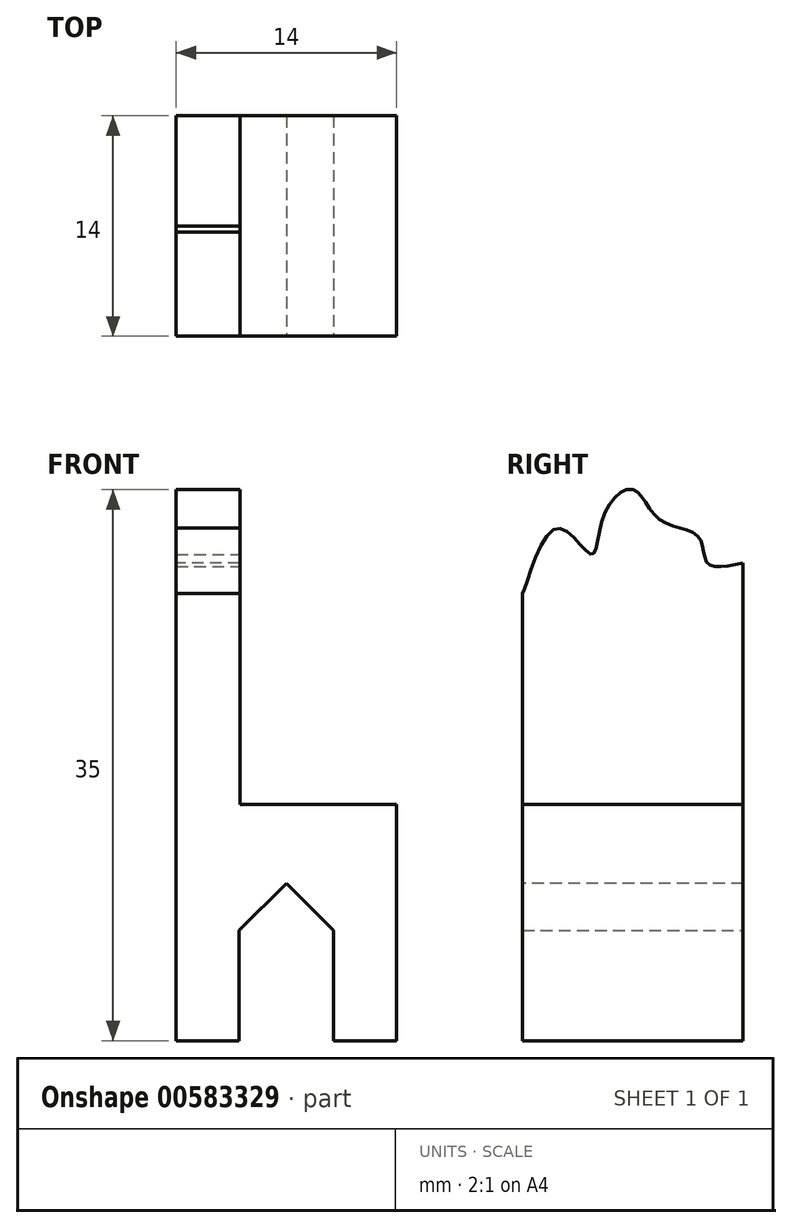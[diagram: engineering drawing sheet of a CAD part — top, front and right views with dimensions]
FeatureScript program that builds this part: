
annotation { "Feature Type Name" : "Feature", "Feature Type Description" : "" }
export const myFeature = defineFeature(function(context is Context, id is Id, definition is map)
    precondition{}
    {
        {
            var Q0;
            Q0=qCreatedBy(makeId("Top.planeOp"),FACE);
            cPlane(context, id + "F0", {"entities" : qUnion([Q0]), "cplaneType" : CPlaneType.OFFSET, "offset" : 6 * mm, "width" : 150 * mm, "height" : 150 * mm});
        }
        {
            var Q0;
            Q0=qCreatedBy(id+"F0.planeOp",FACE);
            var sketch = newSketch(context, id + "F1", { "sketchPlane" : qUnion([Q0])});
            skLineSegment(sketch, "E0.bottom", {"start": v(-111.18, -10.16) * mm, "end": v(-97.18, -10.16) * mm});
            skLineSegment(sketch, "E0.top", {"start": v(-111.18, -24.16) * mm, "end": v(-97.18, -24.16) * mm});
            skLineSegment(sketch, "E0.left", {"start": v(-111.18, -10.16) * mm, "end": v(-111.18, -24.16) * mm});
            skLineSegment(sketch, "E0.right", {"start": v(-97.18, -10.16) * mm, "end": v(-97.18, -24.16) * mm});
            skSolve(sketch);
        }
        {
            var Q0;
            Q0=qSketchRegion(id+"F1",true);
            extrude(context, id + "F2", {"entities" : qUnion([Q0]), "depth" : 15 * mm, "offsetDistance" : 25 * mm});
        }
        {
            var Q0;
            Q0=makeQuery(id+"F2.opExtrude","CAP_FACE",FACE,{"disambiguationData":[OSD([sQuery(id+"F1.wireOp",EDGE,"E0.bottom"),sQuery(id+"F1.wireOp",EDGE,"E0.top"),sQuery(id+"F1.wireOp",EDGE,"E0.left"),sQuery(id+"F1.wireOp",EDGE,"E0.right")])],"isStart":false});
            var sketch = newSketch(context, id + "F3", { "sketchPlane" : qUnion([Q0])});
            skLineSegment(sketch, "E1.bottom", {"start": v(-111.18, -10.16) * mm, "end": v(-107.13, -10.16) * mm});
            skLineSegment(sketch, "E1.top", {"start": v(-111.18, -24.16) * mm, "end": v(-107.13, -24.16) * mm});
            skLineSegment(sketch, "E1.left", {"start": v(-111.18, -10.16) * mm, "end": v(-111.18, -24.16) * mm});
            skLineSegment(sketch, "E1.right", {"start": v(-107.13, -10.16) * mm, "end": v(-107.13, -24.16) * mm});
            skSolve(sketch);
        }
        {
            var Q0;
            Q0=qSketchRegion(id+"F3",true);
            extrude(context, id + "F4", {"entities" : qUnion([Q0]), "operationType" : NewBodyOperationType.ADD, "depth" : 20 * mm, "offsetDistance" : 25 * mm});
        }
        {
            var Q0;
            Q0=makeQuery(id+"F4.boolean.opBoolean","MERGE",FACE,{"derivedFrom":[makeQuery(id+"F2.opExtrude","SWEPT_FACE",FACE,{"disambiguationData":[OSD([sQuery(id+"F1.wireOp",EDGE,"E0.left")])]}),makeQuery(id+"F4.opExtrude","SWEPT_FACE",FACE,{"disambiguationData":[OSD([sQuery(id+"F3.wireOp",EDGE,"E1.left")])]})]});
            var sketch = newSketch(context, id + "F5", { "sketchPlane" : qUnion([Q0])});
            skFitSpline(sketch, "E2", {"points": [v(10.16, 36.34) * mm, v(12.41, 36.34) * mm, v(12.96, 37.99) * mm, v(15.43, 39.09) * mm, v(17.16, 41) * mm, v(19, 39.36) * mm, v(19.83, 36.9) * mm, v(22.02, 38.54) * mm, v(24.16, 34.42) * mm, v(24.16, 35.24) * mm], "startDerivative": vector(26.42, -5.74) * mm, "endDerivative": vector(-1.87, 21.7) * mm});
            skLineSegment(sketch, "E3", {"start": v(10.16, 36.34) * mm, "end": v(10.16, 41) * mm});
            skLineSegment(sketch, "E4", {"start": v(10.16, 41) * mm, "end": v(24.16, 41) * mm});
            skLineSegment(sketch, "E5", {"start": v(24.16, 41) * mm, "end": v(24.2, 34.77) * mm});
            skSolve(sketch);
        }
        {
            var Q0;
            Q0=qSketchRegion(id+"F5",true);
            var Q1;
            {var subQ0=sQuery(id+"F5.wireOp",EDGE,"E4");var subQ1=sQuery(id+"F5.wireOp",EDGE,"E2");var subQ2=makeQuery(id+"F5.imprint","INTERSECT",VERTEX,{"disambiguationData":[OD(1.0)],"derivedFrom":[subQ1,subQ0]});Q1=makeQuery(id+"F5.imprint","IMPRINT",FACE,{"disambiguationData":[TD([[makeQuery(id+"F5.imprint","IMPRINT",EDGE,{"disambiguationData":[TD([[subQ2,-1.0]])],"derivedFrom":subQ1}),1.0]])]});}
            extrude(context, id + "F6", {"entities" : qUnion([Q0, Q1]), "operationType" : NewBodyOperationType.REMOVE, "oppositeDirection" : true, "depth" : 25 * mm, "offsetDistance" : 25 * mm});
        }
        {
            var Q0;
            Q0=makeQuery(id+"F4.boolean.opBoolean","MERGE",FACE,{"derivedFrom":[makeQuery(id+"F2.opExtrude","SWEPT_FACE",FACE,{"disambiguationData":[OSD([sQuery(id+"F1.wireOp",EDGE,"E0.top")])]}),makeQuery(id+"F4.opExtrude","SWEPT_FACE",FACE,{"disambiguationData":[OSD([sQuery(id+"F3.wireOp",EDGE,"E1.top")])]})]});
            var sketch = newSketch(context, id + "F7", { "sketchPlane" : qUnion([Q0])});
            skLineSegment(sketch, "E6", {"start": v(-111.18, 6) * mm, "end": v(-107.18, 6) * mm});
            skLineSegment(sketch, "E7", {"start": v(-97.18, 6) * mm, "end": v(-101.19, 6) * mm});
            skLineSegment(sketch, "E8", {"start": v(-101.19, 6) * mm, "end": v(-101.19, 16) * mm});
            skLineSegment(sketch, "E9", {"start": v(-101.19, 16) * mm, "end": v(-107.18, 16) * mm});
            skLineSegment(sketch, "E10", {"start": v(-107.18, 16) * mm, "end": v(-107.18, 6) * mm});
            skLineSegment(sketch, "E11", {"start": v(-107.18, 6) * mm, "end": v(-101.19, 6) * mm});
            skSolve(sketch);
        }
        {
            var Q0;
            Q0=makeQuery(id+"F7.imprint","IMPRINT",FACE,{"disambiguationData":[TD([[makeQuery(id+"F7.imprint","IMPRINT",EDGE,{"derivedFrom":sQuery(id+"F7.wireOp",EDGE,"E8")}),1.0]])]});
            extrude(context, id + "F8", {"entities" : qUnion([Q0]), "operationType" : NewBodyOperationType.REMOVE, "oppositeDirection" : true, "depth" : 25 * mm, "offsetDistance" : 25 * mm});
        }
        {
            var Q0;
            Q0=makeQuery(id+"F8.boolean.opBoolean","COPY",EDGE,{"derivedFrom":makeQuery(id+"F8.opExtrude","SWEPT_EDGE",EDGE,{"disambiguationData":[OSD([sQuery(id+"F7.wireOp",EDGE,"E9"),sQuery(id+"F7.wireOp",EDGE,"E10")])]})});
            var Q1;
            Q1=makeQuery(id+"F8.boolean.opBoolean","COPY",EDGE,{"derivedFrom":makeQuery(id+"F8.opExtrude","SWEPT_EDGE",EDGE,{"disambiguationData":[OSD([sQuery(id+"F7.wireOp",EDGE,"E8"),sQuery(id+"F7.wireOp",EDGE,"E9")])]})});
            chamfer(context, id + "F9", {"entities" : qUnion([Q0, Q1]), "width" : 3 * mm, "tangentPropagation" : true});
        }
    });
